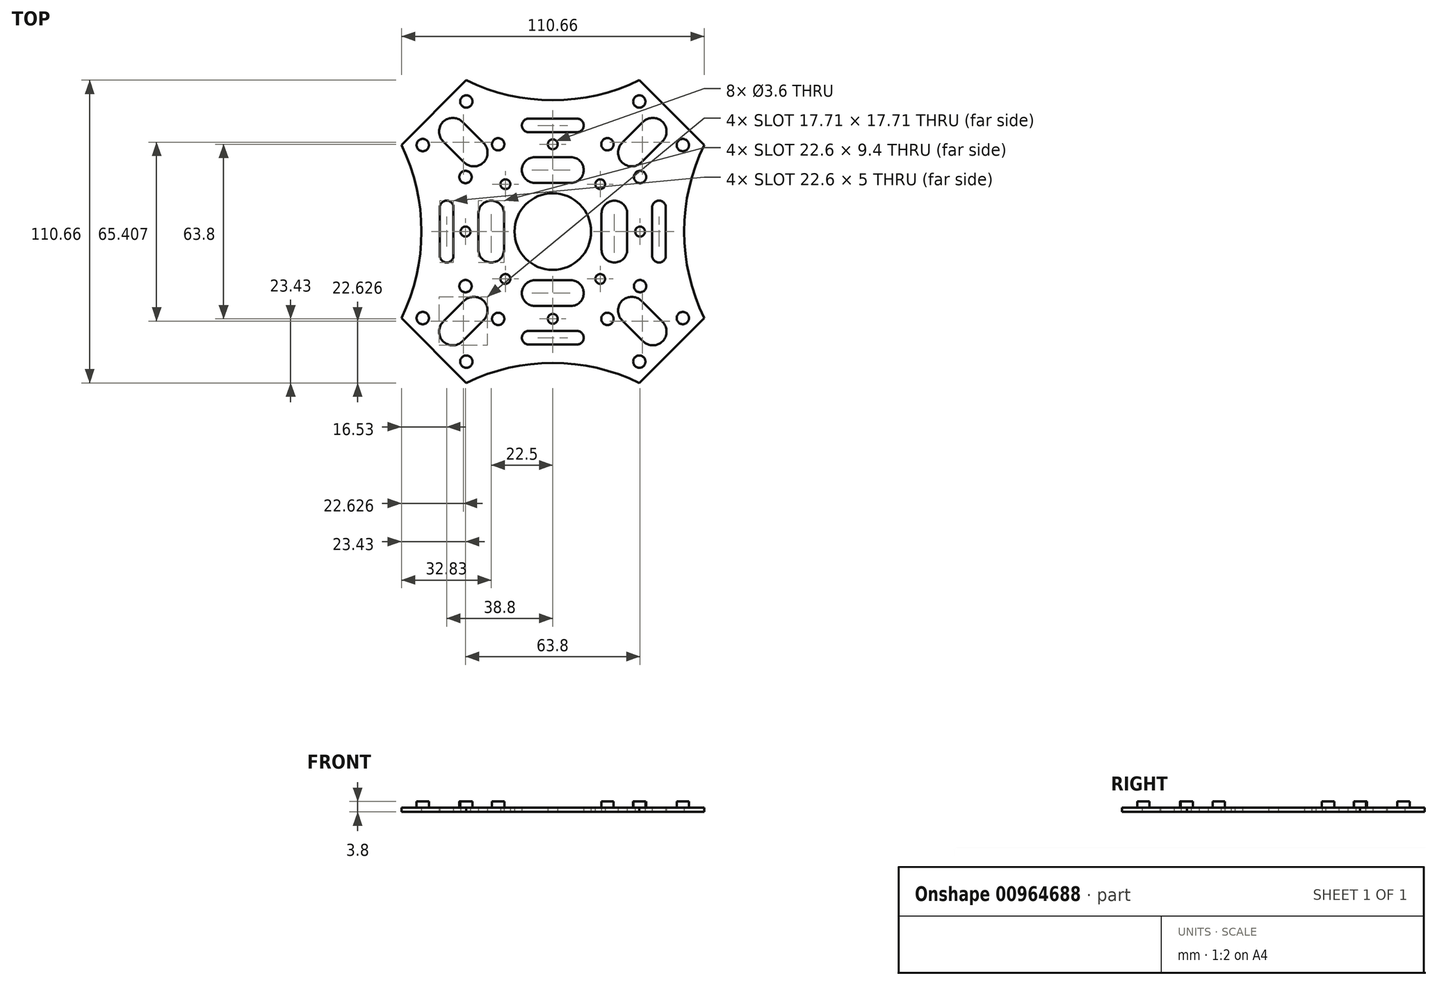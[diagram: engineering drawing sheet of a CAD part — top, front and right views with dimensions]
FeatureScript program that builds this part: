
annotation { "Feature Type Name" : "Feature", "Feature Type Description" : "" }
export const myFeature = defineFeature(function(context is Context, id is Id, definition is map)
    precondition{}
    {
        {
            var Q0;
            Q0=qCreatedBy(makeId("Top.planeOp"),FACE);
            var sketch = newSketch(context, id + "F0", { "sketchPlane" : qUnion([Q0])});
            skCircle(sketch, "E0", {"center": v(0, 0) * mm, "radius": 14 * mm});
            skLineSegment(sketch, "E1", {"start": v(0, 0) * mm, "end": v(83.05, 0) * mm, "construction": true});
            skLineSegment(sketch, "E2", {"start": v(0, 0) * mm, "end": v(67.55, 67.55) * mm, "construction": true});
            skLineSegment(sketch, "E3", {"start": v(17.8, 0) * mm, "end": v(17.8, 6.6) * mm});
            skLineSegment(sketch, "E4", {"start": v(27.2, 0) * mm, "end": v(27.2, 6.6) * mm});
            skArc(sketch, "E5", {"start": v(27.2, 6.6) * mm, "mid": v(22.5, 11.3) * mm, "end": v(17.8, 6.6) * mm});
            skLineSegment(sketch, "E6", {"start": v(36.3, 0) * mm, "end": v(36.3, 8.8) * mm});
            skLineSegment(sketch, "E7", {"start": v(41.3, 0) * mm, "end": v(41.3, 8.8) * mm});
            skArc(sketch, "E8", {"start": v(41.3, 8.8) * mm, "mid": v(38.8, 11.3) * mm, "end": v(36.3, 8.8) * mm});
            skArc(sketch, "E9", {"start": v(33.7, 0) * mm, "mid": v(31.9, 1.8) * mm, "end": v(30.1, 0) * mm});
            skLineSegment(sketch, "E10", {"start": v(32.39, 25.31) * mm, "end": v(40.1, 33.02) * mm});
            skArc(sketch, "E11", {"start": v(32.39, 25.31) * mm, "mid": v(28.85, 23.85) * mm, "end": v(25.31, 25.31) * mm});
            skArc(sketch, "E12", {"start": v(40.1, 33.02) * mm, "mid": v(41.56, 36.56) * mm, "end": v(40.1, 40.1) * mm});
            skLineSegment(sketch, "E13", {"start": v(43.49, 43.49) * mm, "end": v(55.33, 31.64) * mm});
            skArc(sketch, "E14", {"start": v(55.33, 31.64) * mm, "mid": v(49.86, 16.24) * mm, "end": v(48, 0) * mm});
            skArc(sketch, "E15", {"start": v(16.05, 16.05) * mm, "mid": v(18.6, 16.05) * mm, "end": v(18.6, 18.6) * mm});
            skLineSegment(sketch, "E16.MirrorCS", {"start": v(43.49, 43.49) * mm, "end": v(31.64, 55.33) * mm});
            skArc(sketch, "E17.MirrorCS", {"start": v(31.64, 55.33) * mm, "mid": v(16.24, 49.86) * mm, "end": v(0, 48) * mm});
            skArc(sketch, "E18.MirrorCS", {"start": v(33.02, 40.1) * mm, "mid": v(36.56, 41.56) * mm, "end": v(40.1, 40.1) * mm});
            skLineSegment(sketch, "E19.MirrorCS", {"start": v(25.31, 32.39) * mm, "end": v(33.02, 40.1) * mm});
            skArc(sketch, "E20.MirrorCS", {"start": v(25.31, 32.39) * mm, "mid": v(23.85, 28.85) * mm, "end": v(25.31, 25.31) * mm});
            skArc(sketch, "E21.MirrorCS", {"start": v(6.6, 27.2) * mm, "mid": v(11.3, 22.5) * mm, "end": v(6.6, 17.8) * mm});
            skLineSegment(sketch, "E22.MirrorCS", {"start": v(0, 17.8) * mm, "end": v(6.6, 17.8) * mm});
            skLineSegment(sketch, "E23.MirrorCS", {"start": v(0, 27.2) * mm, "end": v(6.6, 27.2) * mm});
            skLineSegment(sketch, "E24.MirrorCS", {"start": v(0, 36.3) * mm, "end": v(8.8, 36.3) * mm});
            skArc(sketch, "E25.MirrorCS", {"start": v(8.8, 41.3) * mm, "mid": v(11.3, 38.8) * mm, "end": v(8.8, 36.3) * mm});
            skLineSegment(sketch, "E26.MirrorCS", {"start": v(0, 41.3) * mm, "end": v(8.8, 41.3) * mm});
            skArc(sketch, "E27.MirrorCS", {"start": v(55.33, -31.64) * mm, "mid": v(49.86, -16.24) * mm, "end": v(48, 0) * mm});
            skLineSegment(sketch, "E28.MirrorCS", {"start": v(41.3, 0) * mm, "end": v(41.3, -8.8) * mm});
            skLineSegment(sketch, "E29.MirrorCS", {"start": v(36.3, 0) * mm, "end": v(36.3, -8.8) * mm});
            skLineSegment(sketch, "E30.MirrorCS", {"start": v(27.2, 0) * mm, "end": v(27.2, -6.6) * mm});
            skLineSegment(sketch, "E31.MirrorCS", {"start": v(17.8, 0) * mm, "end": v(17.8, -6.6) * mm});
            skArc(sketch, "E32.MirrorCS", {"start": v(27.2, -6.6) * mm, "mid": v(22.5, -11.3) * mm, "end": v(17.8, -6.6) * mm});
            skArc(sketch, "E33.MirrorCS", {"start": v(41.3, -8.8) * mm, "mid": v(38.8, -11.3) * mm, "end": v(36.3, -8.8) * mm});
            skLineSegment(sketch, "E34.MirrorCS", {"start": v(32.39, -25.31) * mm, "end": v(40.1, -33.02) * mm});
            skArc(sketch, "E35.MirrorCS", {"start": v(32.39, -25.31) * mm, "mid": v(28.85, -23.85) * mm, "end": v(25.31, -25.31) * mm});
            skArc(sketch, "E36.MirrorCS", {"start": v(25.31, -32.39) * mm, "mid": v(23.85, -28.85) * mm, "end": v(25.31, -25.31) * mm});
            skLineSegment(sketch, "E37.MirrorCS", {"start": v(25.31, -32.39) * mm, "end": v(33.02, -40.1) * mm});
            skArc(sketch, "E38.MirrorCS", {"start": v(33.02, -40.1) * mm, "mid": v(36.56, -41.56) * mm, "end": v(40.1, -40.1) * mm});
            skArc(sketch, "E39.MirrorCS", {"start": v(40.1, -33.02) * mm, "mid": v(41.56, -36.56) * mm, "end": v(40.1, -40.1) * mm});
            skLineSegment(sketch, "E40.MirrorCS", {"start": v(43.49, -43.49) * mm, "end": v(55.33, -31.64) * mm});
            skLineSegment(sketch, "E41.MirrorCS", {"start": v(43.49, -43.49) * mm, "end": v(31.64, -55.33) * mm});
            skArc(sketch, "E42.MirrorCS", {"start": v(31.64, -55.33) * mm, "mid": v(16.24, -49.86) * mm, "end": v(0, -48) * mm});
            skLineSegment(sketch, "E43.MirrorCS", {"start": v(0, -41.3) * mm, "end": v(8.8, -41.3) * mm});
            skArc(sketch, "E44.MirrorCS", {"start": v(8.8, -41.3) * mm, "mid": v(11.3, -38.8) * mm, "end": v(8.8, -36.3) * mm});
            skLineSegment(sketch, "E45.MirrorCS", {"start": v(0, -36.3) * mm, "end": v(8.8, -36.3) * mm});
            skLineSegment(sketch, "E46.MirrorCS", {"start": v(0, -27.2) * mm, "end": v(6.6, -27.2) * mm});
            skArc(sketch, "E47.MirrorCS", {"start": v(6.6, -27.2) * mm, "mid": v(11.3, -22.5) * mm, "end": v(6.6, -17.8) * mm});
            skLineSegment(sketch, "E48.MirrorCS", {"start": v(0, -17.8) * mm, "end": v(6.6, -17.8) * mm});
            skArc(sketch, "E49.MirrorCS", {"start": v(16.05, 16.05) * mm, "mid": v(16.05, 18.6) * mm, "end": v(18.6, 18.6) * mm});
            skArc(sketch, "E50.MirrorCS", {"start": v(33.7, 0) * mm, "mid": v(31.9, -1.8) * mm, "end": v(30.1, 0) * mm});
            skArc(sketch, "E51.MirrorCS", {"start": v(16.05, -16.05) * mm, "mid": v(18.6, -16.05) * mm, "end": v(18.6, -18.6) * mm});
            skArc(sketch, "E52.MirrorCS", {"start": v(16.05, -16.05) * mm, "mid": v(16.05, -18.6) * mm, "end": v(18.6, -18.6) * mm});
            skArc(sketch, "E53.MirrorCS", {"start": v(0, 33.7) * mm, "mid": v(1.8, 31.9) * mm, "end": v(0, 30.1) * mm});
            skArc(sketch, "E54.MirrorCS", {"start": v(0, -33.7) * mm, "mid": v(1.8, -31.9) * mm, "end": v(0, -30.1) * mm});
            skArc(sketch, "E55.MirrorCS", {"start": v(-33.7, 0) * mm, "mid": v(-31.9, -1.8) * mm, "end": v(-30.1, 0) * mm});
            skArc(sketch, "E56.MirrorCS", {"start": v(-33.7, 0) * mm, "mid": v(-31.9, 1.8) * mm, "end": v(-30.1, 0) * mm});
            skArc(sketch, "E57.MirrorCS", {"start": v(-16.05, 16.05) * mm, "mid": v(-18.6, 16.05) * mm, "end": v(-18.6, 18.6) * mm});
            skArc(sketch, "E58.MirrorCS", {"start": v(-16.05, -16.05) * mm, "mid": v(-18.6, -16.05) * mm, "end": v(-18.6, -18.6) * mm});
            skArc(sketch, "E59.MirrorCS", {"start": v(0, -33.7) * mm, "mid": v(-1.8, -31.9) * mm, "end": v(0, -30.1) * mm});
            skArc(sketch, "E60.MirrorCS", {"start": v(-16.05, 16.05) * mm, "mid": v(-16.05, 18.6) * mm, "end": v(-18.6, 18.6) * mm});
            skArc(sketch, "E61.MirrorCS", {"start": v(-16.05, -16.05) * mm, "mid": v(-16.05, -18.6) * mm, "end": v(-18.6, -18.6) * mm});
            skLineSegment(sketch, "E62.MirrorCS", {"start": v(0, 41.3) * mm, "end": v(-8.8, 41.3) * mm});
            skLineSegment(sketch, "E63.MirrorCS", {"start": v(-36.3, 0) * mm, "end": v(-36.3, -8.8) * mm});
            skArc(sketch, "E64.MirrorCS", {"start": v(-41.3, -8.8) * mm, "mid": v(-38.8, -11.3) * mm, "end": v(-36.3, -8.8) * mm});
            skArc(sketch, "E65.MirrorCS", {"start": v(-27.2, -6.6) * mm, "mid": v(-22.5, -11.3) * mm, "end": v(-17.8, -6.6) * mm});
            skLineSegment(sketch, "E66.MirrorCS", {"start": v(0, -27.2) * mm, "end": v(-6.6, -27.2) * mm});
            skLineSegment(sketch, "E67.MirrorCS", {"start": v(-36.3, 0) * mm, "end": v(-36.3, 8.8) * mm});
            skLineSegment(sketch, "E68.MirrorCS", {"start": v(-25.31, 32.39) * mm, "end": v(-33.02, 40.1) * mm});
            skLineSegment(sketch, "E69.MirrorCS", {"start": v(0, 36.3) * mm, "end": v(-8.8, 36.3) * mm});
            skLineSegment(sketch, "E70.MirrorCS", {"start": v(0, 17.8) * mm, "end": v(-6.6, 17.8) * mm});
            skLineSegment(sketch, "E71.MirrorCS", {"start": v(-27.2, 0) * mm, "end": v(-27.2, 6.6) * mm});
            skArc(sketch, "E72.MirrorCS", {"start": v(-8.8, 41.3) * mm, "mid": v(-11.3, 38.8) * mm, "end": v(-8.8, 36.3) * mm});
            skArc(sketch, "E73.MirrorCS", {"start": v(0, 33.7) * mm, "mid": v(-1.8, 31.9) * mm, "end": v(0, 30.1) * mm});
            skLineSegment(sketch, "E74.MirrorCS", {"start": v(-27.2, 0) * mm, "end": v(-27.2, -6.6) * mm});
            skArc(sketch, "E75.MirrorCS", {"start": v(-6.6, 27.2) * mm, "mid": v(-11.3, 22.5) * mm, "end": v(-6.6, 17.8) * mm});
            skLineSegment(sketch, "E76.MirrorCS", {"start": v(0, -36.3) * mm, "end": v(-8.8, -36.3) * mm});
            skArc(sketch, "E77.MirrorCS", {"start": v(-27.2, 6.6) * mm, "mid": v(-22.5, 11.3) * mm, "end": v(-17.8, 6.6) * mm});
            skArc(sketch, "E78.MirrorCS", {"start": v(-25.31, 32.39) * mm, "mid": v(-23.85, 28.85) * mm, "end": v(-25.31, 25.31) * mm});
            skLineSegment(sketch, "E79.MirrorCS", {"start": v(-43.49, -43.49) * mm, "end": v(-31.64, -55.33) * mm});
            skArc(sketch, "E80.MirrorCS", {"start": v(-40.1, -33.02) * mm, "mid": v(-41.56, -36.56) * mm, "end": v(-40.1, -40.1) * mm});
            skLineSegment(sketch, "E81.MirrorCS", {"start": v(-43.49, 43.49) * mm, "end": v(-31.64, 55.33) * mm});
            skLineSegment(sketch, "E82.MirrorCS", {"start": v(-17.8, 0) * mm, "end": v(-17.8, 6.6) * mm});
            skArc(sketch, "E83.MirrorCS", {"start": v(-32.39, 25.31) * mm, "mid": v(-28.85, 23.85) * mm, "end": v(-25.31, 25.31) * mm});
            skArc(sketch, "E84.MirrorCS", {"start": v(-33.02, 40.1) * mm, "mid": v(-36.56, 41.56) * mm, "end": v(-40.1, 40.1) * mm});
            skArc(sketch, "E85.MirrorCS", {"start": v(-33.02, -40.1) * mm, "mid": v(-36.56, -41.56) * mm, "end": v(-40.1, -40.1) * mm});
            skLineSegment(sketch, "E86.MirrorCS", {"start": v(-17.8, 0) * mm, "end": v(-17.8, -6.6) * mm});
            skLineSegment(sketch, "E87.MirrorCS", {"start": v(-41.3, 0) * mm, "end": v(-41.3, 8.8) * mm});
            skArc(sketch, "E88.MirrorCS", {"start": v(-40.1, 33.02) * mm, "mid": v(-41.56, 36.56) * mm, "end": v(-40.1, 40.1) * mm});
            skArc(sketch, "E89.MirrorCS", {"start": v(-31.64, -55.33) * mm, "mid": v(-16.24, -49.86) * mm, "end": v(0, -48) * mm});
            skLineSegment(sketch, "E90.MirrorCS", {"start": v(-41.3, 0) * mm, "end": v(-41.3, -8.8) * mm});
            skArc(sketch, "E91.MirrorCS", {"start": v(-31.64, 55.33) * mm, "mid": v(-16.24, 49.86) * mm, "end": v(0, 48) * mm});
            skArc(sketch, "E92.MirrorCS", {"start": v(-6.6, -27.2) * mm, "mid": v(-11.3, -22.5) * mm, "end": v(-6.6, -17.8) * mm});
            skLineSegment(sketch, "E93.MirrorCS", {"start": v(-43.49, -43.49) * mm, "end": v(-55.33, -31.64) * mm});
            skArc(sketch, "E94.MirrorCS", {"start": v(-55.33, 31.64) * mm, "mid": v(-49.86, 16.24) * mm, "end": v(-48, 0) * mm});
            skArc(sketch, "E95.MirrorCS", {"start": v(-25.31, -32.39) * mm, "mid": v(-23.85, -28.85) * mm, "end": v(-25.31, -25.31) * mm});
            skArc(sketch, "E96.MirrorCS", {"start": v(-55.33, -31.64) * mm, "mid": v(-49.86, -16.24) * mm, "end": v(-48, 0) * mm});
            skArc(sketch, "E97.MirrorCS", {"start": v(-32.39, -25.31) * mm, "mid": v(-28.85, -23.85) * mm, "end": v(-25.31, -25.31) * mm});
            skArc(sketch, "E98.MirrorCS", {"start": v(-8.8, -41.3) * mm, "mid": v(-11.3, -38.8) * mm, "end": v(-8.8, -36.3) * mm});
            skLineSegment(sketch, "E99.MirrorCS", {"start": v(-25.31, -32.39) * mm, "end": v(-33.02, -40.1) * mm});
            skLineSegment(sketch, "E100.MirrorCS", {"start": v(-43.49, 43.49) * mm, "end": v(-55.33, 31.64) * mm});
            skArc(sketch, "E101.MirrorCS", {"start": v(-41.3, 8.8) * mm, "mid": v(-38.8, 11.3) * mm, "end": v(-36.3, 8.8) * mm});
            skLineSegment(sketch, "E102.MirrorCS", {"start": v(0, 27.2) * mm, "end": v(-6.6, 27.2) * mm});
            skLineSegment(sketch, "E103.MirrorCS", {"start": v(0, -41.3) * mm, "end": v(-8.8, -41.3) * mm});
            skLineSegment(sketch, "E104.MirrorCS", {"start": v(-32.39, 25.31) * mm, "end": v(-40.1, 33.02) * mm});
            skLineSegment(sketch, "E105.MirrorCS", {"start": v(0, -17.8) * mm, "end": v(-6.6, -17.8) * mm});
            skLineSegment(sketch, "E106.MirrorCS", {"start": v(-32.39, -25.31) * mm, "end": v(-40.1, -33.02) * mm});
            skSolve(sketch);
        }
        {
            var Q0;
            Q0=makeQuery(id+"F0.imprint","IMPRINT",FACE,{"disambiguationData":[TD([[makeQuery(id+"F0.imprint","IMPRINT",EDGE,{"derivedFrom":sQuery(id+"F0.wireOp",EDGE,"E3")}),1.0]])]});
            extrude(context, id + "F1", {"entities" : qUnion([Q0]), "depth" : 1.6 * mm, "offsetDistance" : 25 * mm});
        }
        {
            var Q0;
            Q0=makeQuery(id+"F1.opExtrude","CAP_FACE",FACE,{"disambiguationData":[OSD([sQuery(id+"F0.wireOp",EDGE,"E3"),sQuery(id+"F0.wireOp",EDGE,"E4"),sQuery(id+"F0.wireOp",EDGE,"E5"),sQuery(id+"F0.wireOp",EDGE,"E6"),sQuery(id+"F0.wireOp",EDGE,"E7"),sQuery(id+"F0.wireOp",EDGE,"E8"),sQuery(id+"F0.wireOp",EDGE,"E9"),sQuery(id+"F0.wireOp",EDGE,"E10"),sQuery(id+"F0.wireOp",EDGE,"E11"),sQuery(id+"F0.wireOp",EDGE,"E12"),sQuery(id+"F0.wireOp",EDGE,"E13"),sQuery(id+"F0.wireOp",EDGE,"E14"),sQuery(id+"F0.wireOp",EDGE,"E15"),sQuery(id+"F0.wireOp",EDGE,"E16.MirrorCS"),sQuery(id+"F0.wireOp",EDGE,"E17.MirrorCS"),sQuery(id+"F0.wireOp",EDGE,"E18.MirrorCS"),sQuery(id+"F0.wireOp",EDGE,"E19.MirrorCS"),sQuery(id+"F0.wireOp",EDGE,"E20.MirrorCS"),sQuery(id+"F0.wireOp",EDGE,"E21.MirrorCS"),sQuery(id+"F0.wireOp",EDGE,"E22.MirrorCS"),sQuery(id+"F0.wireOp",EDGE,"E23.MirrorCS"),sQuery(id+"F0.wireOp",EDGE,"E24.MirrorCS"),sQuery(id+"F0.wireOp",EDGE,"E25.MirrorCS"),sQuery(id+"F0.wireOp",EDGE,"E26.MirrorCS"),sQuery(id+"F0.wireOp",EDGE,"E27.MirrorCS"),sQuery(id+"F0.wireOp",EDGE,"E28.MirrorCS"),sQuery(id+"F0.wireOp",EDGE,"E29.MirrorCS"),sQuery(id+"F0.wireOp",EDGE,"E30.MirrorCS"),sQuery(id+"F0.wireOp",EDGE,"E31.MirrorCS"),sQuery(id+"F0.wireOp",EDGE,"E32.MirrorCS"),sQuery(id+"F0.wireOp",EDGE,"E33.MirrorCS"),sQuery(id+"F0.wireOp",EDGE,"E34.MirrorCS"),sQuery(id+"F0.wireOp",EDGE,"E35.MirrorCS"),sQuery(id+"F0.wireOp",EDGE,"E36.MirrorCS"),sQuery(id+"F0.wireOp",EDGE,"E37.MirrorCS"),sQuery(id+"F0.wireOp",EDGE,"E38.MirrorCS"),sQuery(id+"F0.wireOp",EDGE,"E39.MirrorCS"),sQuery(id+"F0.wireOp",EDGE,"E40.MirrorCS"),sQuery(id+"F0.wireOp",EDGE,"E41.MirrorCS"),sQuery(id+"F0.wireOp",EDGE,"E42.MirrorCS"),sQuery(id+"F0.wireOp",EDGE,"E43.MirrorCS"),sQuery(id+"F0.wireOp",EDGE,"E44.MirrorCS"),sQuery(id+"F0.wireOp",EDGE,"E45.MirrorCS"),sQuery(id+"F0.wireOp",EDGE,"E46.MirrorCS"),sQuery(id+"F0.wireOp",EDGE,"E47.MirrorCS"),sQuery(id+"F0.wireOp",EDGE,"E48.MirrorCS"),sQuery(id+"F0.wireOp",EDGE,"E49.MirrorCS"),sQuery(id+"F0.wireOp",EDGE,"E50.MirrorCS"),sQuery(id+"F0.wireOp",EDGE,"E51.MirrorCS"),sQuery(id+"F0.wireOp",EDGE,"E52.MirrorCS"),sQuery(id+"F0.wireOp",EDGE,"E53.MirrorCS"),sQuery(id+"F0.wireOp",EDGE,"E54.MirrorCS"),sQuery(id+"F0.wireOp",EDGE,"E55.MirrorCS"),sQuery(id+"F0.wireOp",EDGE,"E56.MirrorCS"),sQuery(id+"F0.wireOp",EDGE,"E57.MirrorCS"),sQuery(id+"F0.wireOp",EDGE,"E58.MirrorCS"),sQuery(id+"F0.wireOp",EDGE,"E59.MirrorCS"),sQuery(id+"F0.wireOp",EDGE,"E60.MirrorCS"),sQuery(id+"F0.wireOp",EDGE,"E61.MirrorCS"),sQuery(id+"F0.wireOp",EDGE,"E62.MirrorCS"),sQuery(id+"F0.wireOp",EDGE,"E63.MirrorCS"),sQuery(id+"F0.wireOp",EDGE,"E64.MirrorCS"),sQuery(id+"F0.wireOp",EDGE,"E65.MirrorCS"),sQuery(id+"F0.wireOp",EDGE,"E66.MirrorCS"),sQuery(id+"F0.wireOp",EDGE,"E67.MirrorCS"),sQuery(id+"F0.wireOp",EDGE,"E68.MirrorCS"),sQuery(id+"F0.wireOp",EDGE,"E69.MirrorCS"),sQuery(id+"F0.wireOp",EDGE,"E70.MirrorCS"),sQuery(id+"F0.wireOp",EDGE,"E71.MirrorCS"),sQuery(id+"F0.wireOp",EDGE,"E72.MirrorCS"),sQuery(id+"F0.wireOp",EDGE,"E73.MirrorCS"),sQuery(id+"F0.wireOp",EDGE,"E74.MirrorCS"),sQuery(id+"F0.wireOp",EDGE,"E75.MirrorCS"),sQuery(id+"F0.wireOp",EDGE,"E76.MirrorCS"),sQuery(id+"F0.wireOp",EDGE,"E77.MirrorCS"),sQuery(id+"F0.wireOp",EDGE,"E78.MirrorCS"),sQuery(id+"F0.wireOp",EDGE,"E79.MirrorCS"),sQuery(id+"F0.wireOp",EDGE,"E80.MirrorCS"),sQuery(id+"F0.wireOp",EDGE,"E81.MirrorCS"),sQuery(id+"F0.wireOp",EDGE,"E82.MirrorCS"),sQuery(id+"F0.wireOp",EDGE,"E83.MirrorCS"),sQuery(id+"F0.wireOp",EDGE,"E84.MirrorCS"),sQuery(id+"F0.wireOp",EDGE,"E85.MirrorCS"),sQuery(id+"F0.wireOp",EDGE,"E86.MirrorCS"),sQuery(id+"F0.wireOp",EDGE,"E87.MirrorCS"),sQuery(id+"F0.wireOp",EDGE,"E88.MirrorCS"),sQuery(id+"F0.wireOp",EDGE,"E89.MirrorCS"),sQuery(id+"F0.wireOp",EDGE,"E90.MirrorCS"),sQuery(id+"F0.wireOp",EDGE,"E91.MirrorCS"),sQuery(id+"F0.wireOp",EDGE,"E92.MirrorCS"),sQuery(id+"F0.wireOp",EDGE,"E93.MirrorCS"),sQuery(id+"F0.wireOp",EDGE,"E94.MirrorCS"),sQuery(id+"F0.wireOp",EDGE,"E95.MirrorCS"),sQuery(id+"F0.wireOp",EDGE,"E96.MirrorCS"),sQuery(id+"F0.wireOp",EDGE,"E97.MirrorCS"),sQuery(id+"F0.wireOp",EDGE,"E98.MirrorCS"),sQuery(id+"F0.wireOp",EDGE,"E99.MirrorCS"),sQuery(id+"F0.wireOp",EDGE,"E100.MirrorCS"),sQuery(id+"F0.wireOp",EDGE,"E101.MirrorCS"),sQuery(id+"F0.wireOp",EDGE,"E102.MirrorCS"),sQuery(id+"F0.wireOp",EDGE,"E103.MirrorCS"),sQuery(id+"F0.wireOp",EDGE,"E104.MirrorCS"),sQuery(id+"F0.wireOp",EDGE,"E105.MirrorCS"),sQuery(id+"F0.wireOp",EDGE,"E106.MirrorCS"),sQuery(id+"F0.wireOp",EDGE,"E0")])],"isStart":false});
            var sketch = newSketch(context, id + "F2", { "sketchPlane" : qUnion([Q0])});
            skCircle(sketch, "E107", {"center": v(31.9, 19.95) * mm, "radius": 2.25 * mm});
            skCircle(sketch, "E108", {"center": v(47.53, 31.62) * mm, "radius": 2.25 * mm});
            skCircle(sketch, "E109.MirrorC", {"center": v(31.62, 47.53) * mm, "radius": 2.25 * mm});
            skCircle(sketch, "E110.MirrorC", {"center": v(19.95, 31.9) * mm, "radius": 2.25 * mm});
            skCircle(sketch, "E111.MirrorC", {"center": v(47.53, -31.62) * mm, "radius": 2.25 * mm});
            skCircle(sketch, "E112.MirrorC", {"center": v(31.9, -19.95) * mm, "radius": 2.25 * mm});
            skCircle(sketch, "E113.MirrorC", {"center": v(19.95, -31.9) * mm, "radius": 2.25 * mm});
            skCircle(sketch, "E114.MirrorC", {"center": v(31.62, -47.53) * mm, "radius": 2.25 * mm});
            skCircle(sketch, "E115.MirrorC", {"center": v(-31.9, -19.95) * mm, "radius": 2.25 * mm});
            skCircle(sketch, "E116.MirrorC", {"center": v(-31.9, 19.95) * mm, "radius": 2.25 * mm});
            skCircle(sketch, "E117.MirrorC", {"center": v(-47.53, -31.62) * mm, "radius": 2.25 * mm});
            skCircle(sketch, "E118.MirrorC", {"center": v(-31.62, 47.53) * mm, "radius": 2.25 * mm});
            skCircle(sketch, "E119.MirrorC", {"center": v(-47.53, 31.62) * mm, "radius": 2.25 * mm});
            skCircle(sketch, "E120.MirrorC", {"center": v(-31.62, -47.53) * mm, "radius": 2.25 * mm});
            skCircle(sketch, "E121.MirrorC", {"center": v(-19.95, 31.9) * mm, "radius": 2.25 * mm});
            skCircle(sketch, "E122.MirrorC", {"center": v(-19.95, -31.9) * mm, "radius": 2.25 * mm});
            skSolve(sketch);
        }
        {
            var Q0;
            Q0=qSketchRegion(id+"F2",true);
            extrude(context, id + "F3", {"entities" : qUnion([Q0]), "operationType" : NewBodyOperationType.ADD, "depth" : 2.2 * mm, "offsetDistance" : 25 * mm});
        }
    });
